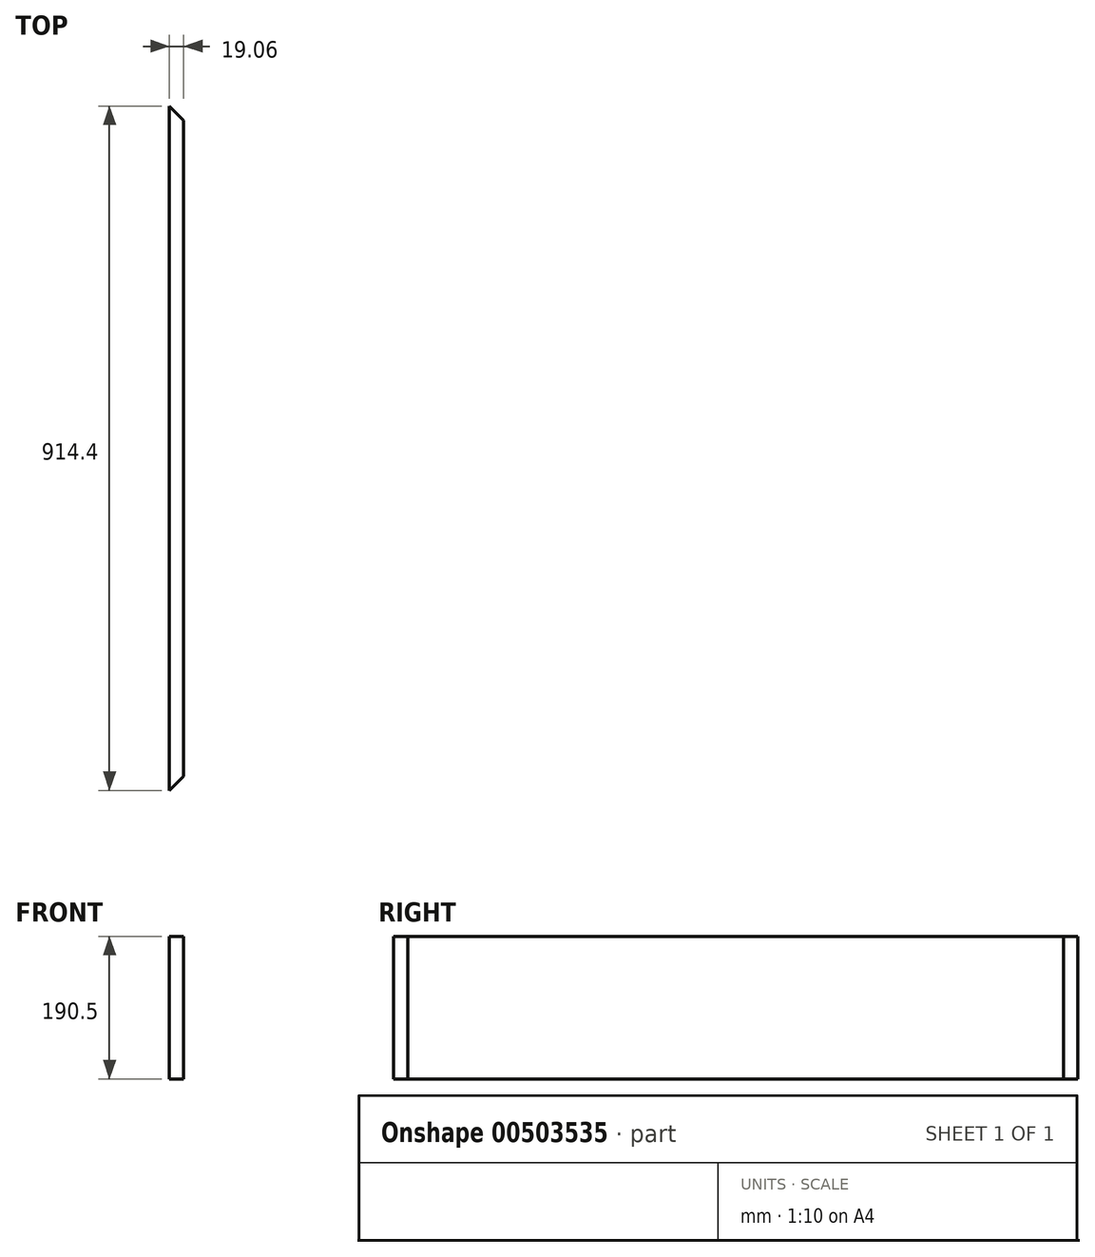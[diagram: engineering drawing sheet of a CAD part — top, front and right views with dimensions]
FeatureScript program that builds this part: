
annotation { "Feature Type Name" : "Feature", "Feature Type Description" : "" }
export const myFeature = defineFeature(function(context is Context, id is Id, definition is map)
    precondition{}
    {
        {
            var Q0;
            Q0=qCreatedBy(makeId("Front.planeOp"),FACE);
            var sketch = newSketch(context, id + "F0", { "sketchPlane" : qUnion([Q0])});
            skLineSegment(sketch, "E0.bottom", {"start": v(-9.53, 95.25) * mm, "end": v(9.53, 95.25) * mm});
            skLineSegment(sketch, "E0.top", {"start": v(-9.53, -95.25) * mm, "end": v(9.53, -95.25) * mm});
            skLineSegment(sketch, "E0.left", {"start": v(-9.52, 95.25) * mm, "end": v(-9.53, -95.25) * mm});
            skLineSegment(sketch, "E0.right", {"start": v(9.53, 95.25) * mm, "end": v(9.52, -95.25) * mm});
            skLineSegment(sketch, "E1", {"start": v(50, 0) * mm, "end": v(-52.25, 0) * mm});
            skLineSegment(sketch, "E2", {"start": v(0, 55) * mm, "end": v(0, -99.5) * mm});
            skSolve(sketch);
        }
        {
            var Q0;
            Q0 = qSketchRegion(id + "F0", true);
            extrude(context, id + "F1", {"entities" : qUnion([Q0]), "endBound" : BoundingType.SYMMETRIC, "depth" : 914.4 * mm});
        }
        {
            var Q0;
            Q0=makeQuery(id+"F1.opExtrude","CAP_EDGE",EDGE,{"disambiguationData":[OSD([sQuery(id+"F0.wireOp",EDGE,"E0.right")])],"isStart":false});
            var Q1;
            Q1=makeQuery(id+"F1.opExtrude","CAP_EDGE",EDGE,{"disambiguationData":[OSD([sQuery(id+"F0.wireOp",EDGE,"E0.right")])],"isStart":true});
            chamfer(context, id + "F2", {"entities" : qUnion([Q0, Q1]), "width" : 19.05 * mm, "tangentPropagation" : true});
        }
    });
